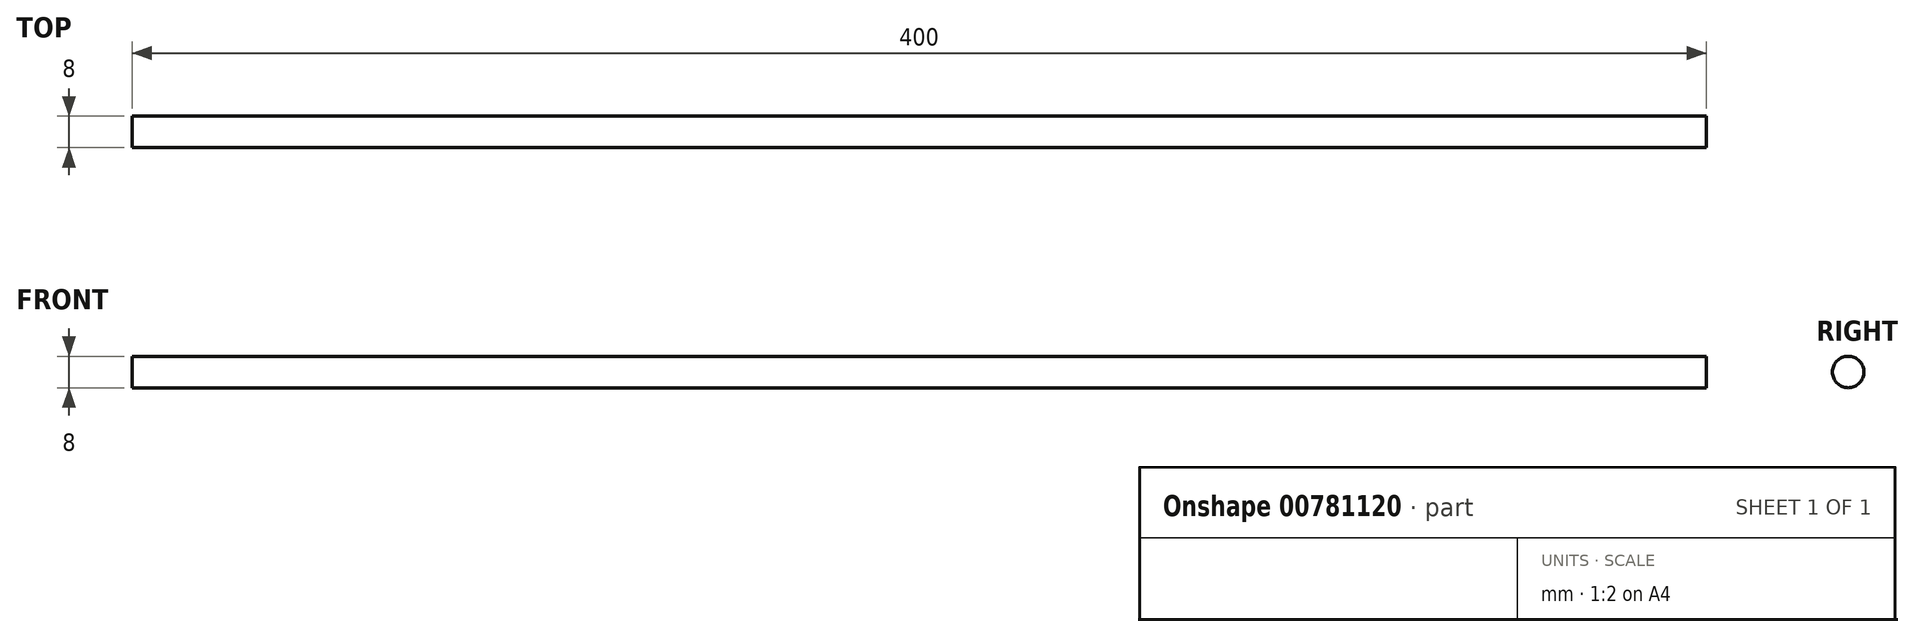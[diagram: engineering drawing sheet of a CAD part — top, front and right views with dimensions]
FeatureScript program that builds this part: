
annotation { "Feature Type Name" : "Feature", "Feature Type Description" : "" }
export const myFeature = defineFeature(function(context is Context, id is Id, definition is map)
    precondition{}
    {
        {
            var Q0;
            Q0=qCreatedBy(makeId("Right.planeOp"),FACE);
            var sketch = newSketch(context, id + "F0", { "sketchPlane" : qUnion([Q0])});
            skCircle(sketch, "E0", {"center": v(0, 0) * mm, "radius": 4 * mm});
            skSolve(sketch);
        }
        {
            var Q0;
            Q0 = qSketchRegion(id + "F0", true);
            extrude(context, id + "F1", {"entities" : qUnion([Q0]), "depth" : 400 * mm, "offsetDistance" : 25 * mm});
        }
    });
